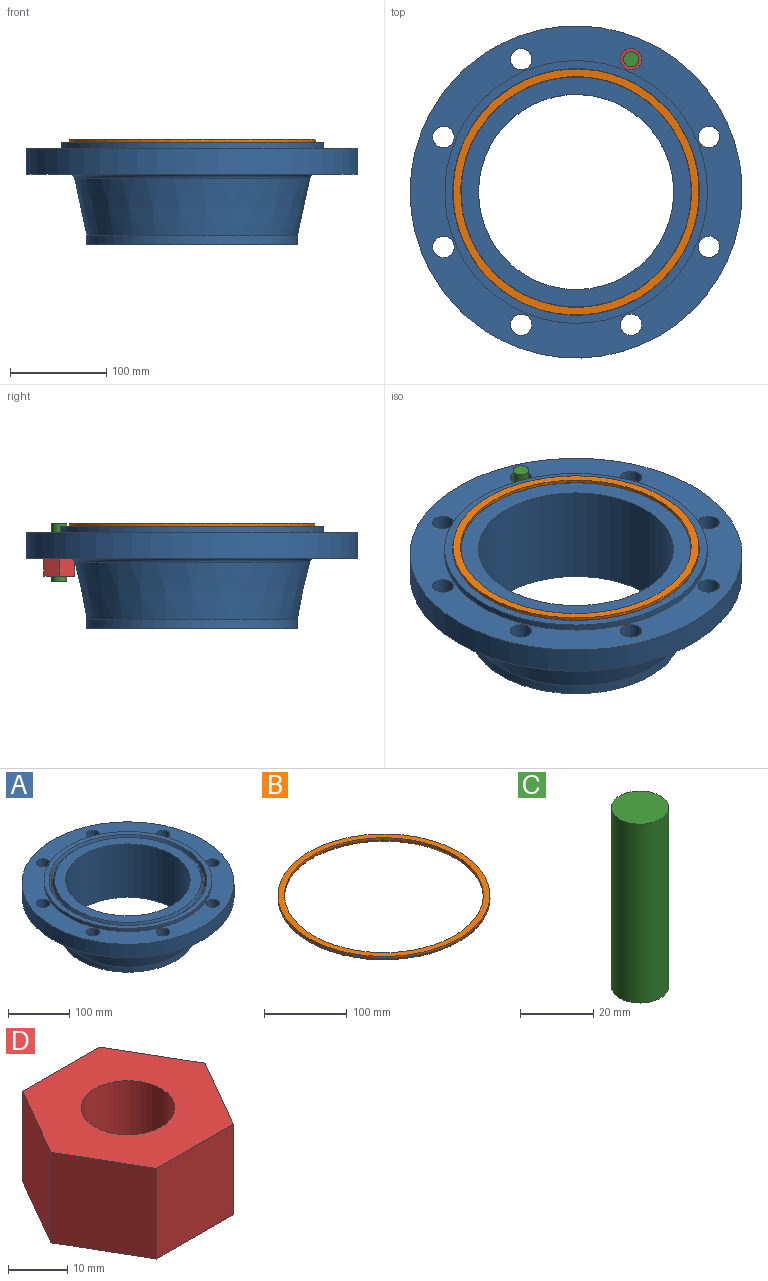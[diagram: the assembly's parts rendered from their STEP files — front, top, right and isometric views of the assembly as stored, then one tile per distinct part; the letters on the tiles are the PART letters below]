
ASSEMBLY  parts=4 mates=5
PART A: 24 faces, bbox 345x345x106.4 mm
  f0: plane 238.91x238.91mm, normal (0,0,1), area 12559.1mm2, adj f1,f20
  f1: cylinder r=101.35mm len=202.7mm, axis (0,0,-1), area 67723.8mm2, adj f0,f2
  f2: plane 219.1x219.1mm, normal (0,0,-1), area 5433mm2, adj f1,f3
  f3: cylinder r=109.55mm len=219.1mm, axis (0,0,-1), area 6883.2mm2, adj f2,f4
  f4: cone r=123mm half-angle=12.1deg, axis (0,0,1), area 43948.1mm2, adj f3,f16
  f5: plane 345x345mm, normal (0,0,-1), area 39671.6mm2, adj f6,f8,f9,f10,f11,f12,f13,f14
  f6: cylinder r=172.5mm len=345mm, axis (0,0,-1), area 29263.9mm2, adj f5,f7
  f7: plane 345x345mm, normal (0,0,1), area 31843.5mm2, adj f6,f8,f9,f10,f11,f12,f13,f14
  f8: cylinder r=11.11mm len=27mm, axis (0,0,1), area 1885.2mm2, adj f5,f7
  f9: cylinder r=11.11mm len=27mm, axis (0,0,1), area 1885.2mm2, adj f5,f7
  f10: cylinder r=11.11mm len=27mm, axis (0,0,1), area 1885.2mm2, adj f5,f7
  f11: cylinder r=11.11mm len=27mm, axis (0,0,1), area 1885.2mm2, adj f5,f7
  f12: cylinder r=11.11mm len=27mm, axis (0,0,1), area 1885.2mm2, adj f5,f7
  f13: cylinder r=11.11mm len=27mm, axis (0,0,1), area 1885.2mm2, adj f5,f7
  f14: cylinder r=11.11mm len=27mm, axis (0,0,1), area 1885.2mm2, adj f5,f7
  f15: cylinder r=11.11mm len=27mm, axis (0,0,1), area 1885.2mm2, adj f5,f7
  f16: torus R=127.05mm, axis (0,0,1), area 5305.7mm2, adj f4,f5
  f17: cylinder r=136.5mm len=273mm, axis (0,0,-1), area 5446.1mm2, adj f7,f18
  f18: plane 273x273mm, normal (0,0,1), area 6906.1mm2, adj f17,f19
  f19: cone r=128.19mm half-angle=23deg, axis (0,0,1), area 5080.2mm2, adj f18,f23
  f20: cone r=119.46mm half-angle=23deg, axis (0,0,-1), area 4830mm2, adj f0,f21
  f21: torus R=122.68mm, axis (0,0,1), area 718.6mm2, adj f20,f22
  f22: plane 249.94x249.94mm, normal (0,0,1), area 1781.8mm2, adj f21,f23
  f23: torus R=124.97mm, axis (0,0,1), area 737mm2, adj f19,f22
PART B: 5 faces, bbox 276.7x276.7x7.1 mm
  f0: cylinder r=127.8mm len=255.6mm, axis (0,0,-1), area 2509.3mm2, adj f3,f4
  f1: cylinder r=119.85mm len=239.7mm, axis (0,0,-1), area 2353.2mm2, adj f2,f4
  f2: torus R=123.83mm, axis (0,0,-1), area 8435.5mm2, adj f1,f3
  f3: torus R=123.83mm, axis (0,0,-1), area 1280.2mm2, adj f0,f2
  f4: plane 255.6x255.6mm, normal (0,0,1), area 6185.2mm2, adj f0,f1
PART C: 3 faces, bbox 15.8x15.8x60 mm
  f0: cylinder r=7.88mm len=60mm, axis (0,0,-1), area 2968.8mm2, adj f1,f2
  f1: plane 15.75x15.75mm, normal (0,0,1), area 194.8mm2, adj f0
  f2: plane 15.75x15.75mm, normal (0,0,-1), area 194.8mm2, adj f0
PART D: 9 faces, bbox 36.7x31.8x18.7 mm
  f0: plane 18.65x18.33mm, normal (0,-1,0), area 341.9mm2, adj f1,f5,f6,f7
  f1: plane 18.65x15.88mm, normal (0.87,-0.5,0), area 341.9mm2, adj f0,f2,f6,f7
  f2: plane 18.65x15.88mm, normal (0.87,0.5,0), area 341.9mm2, adj f1,f3,f6,f7
  f3: plane 18.65x18.33mm, normal (0,1,0), area 341.9mm2, adj f2,f4,f6,f7
  f4: plane 18.65x15.88mm, normal (-0.87,0.5,0), area 341.9mm2, adj f3,f5,f6,f7
  f5: plane 18.65x15.88mm, normal (-0.87,-0.5,0), area 341.9mm2, adj f0,f4,f6,f7
  f6: plane 36.66x31.75mm, normal (0,0,1), area 678.2mm2, adj f0,f1,f2,f3,f4,f5,f8
  f7: plane 36.66x31.75mm, normal (0,0,-1), area 678.2mm2, adj f0,f1,f2,f3,f4,f5,f8
  f8: cylinder r=7.88mm len=18.65mm, axis (0,0,1), area 922.8mm2, adj f6,f7
PLACE A at identity fixed
PLACE B rot(axis=(0,0,1),10.5deg) t=(0,0,106.23)mm
PLACE C t=(57.12,137.89,49.35)mm
PLACE D t=(57.12,137.89,54.35)mm
MATE cylindrical D.f8 <-> A.f8  axis (0,0,1) through (57.12,137.89,73)mm
MATE cylindrical A.f8 <-> C.f0  axis (0,0,1) through (57.12,137.89,100)mm
MATE cylindrical B.f0 <-> A.f1  axis (0,0,-1) through (0,0,107.79)mm
MATE planar C.f0 <-> B.f0  axis (0,0,1) through (57.12,137.89,109.35)mm
MATE planar A.f1 <-> D.f6  axis (0,0,-1) through (0,0,73)mm
